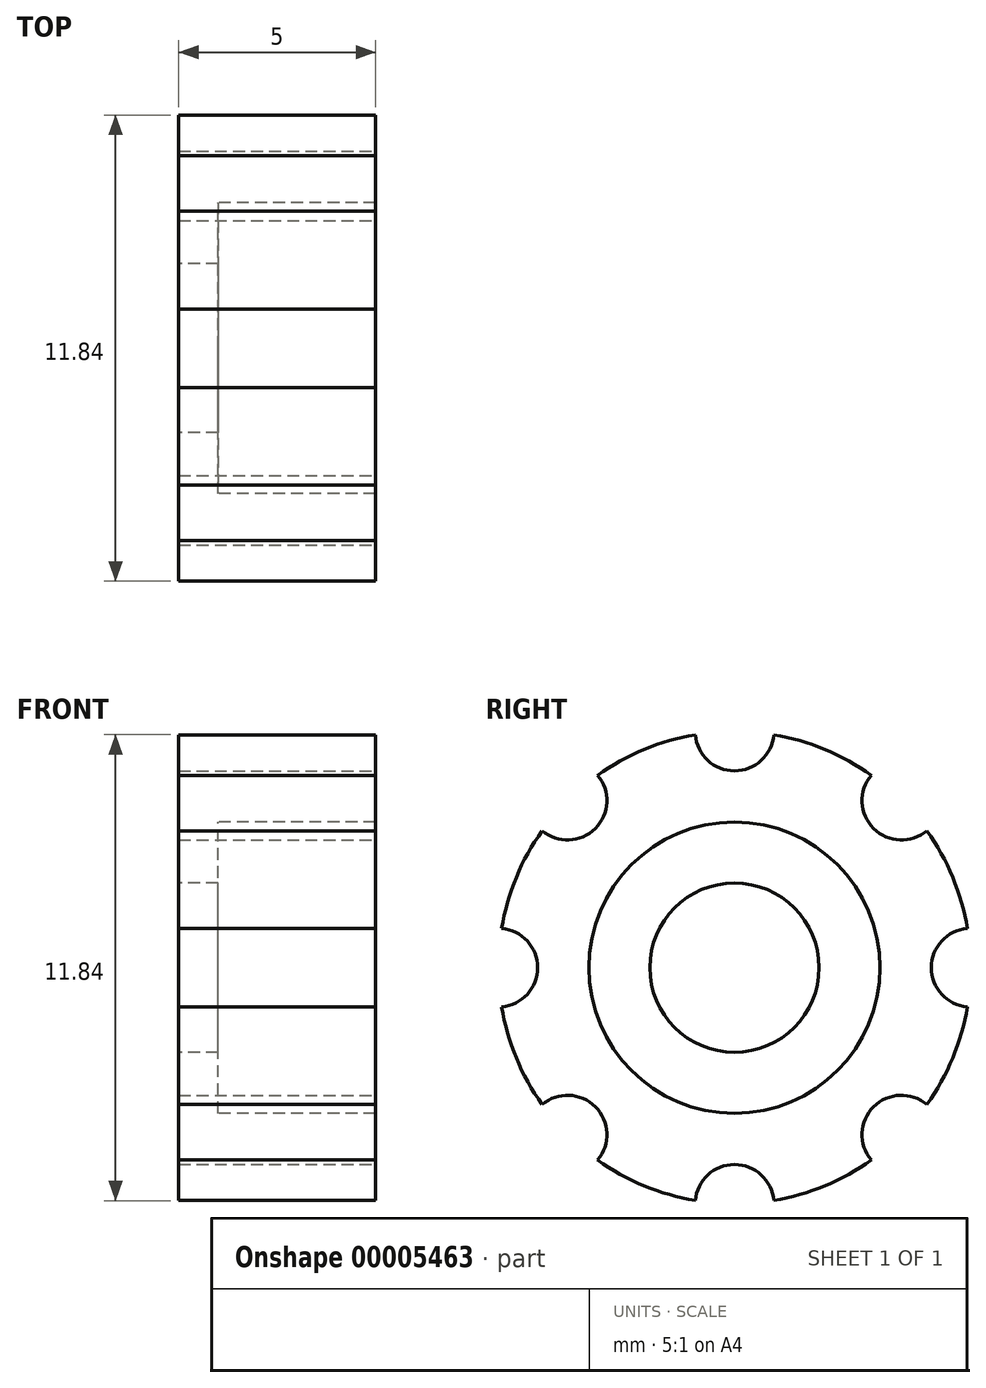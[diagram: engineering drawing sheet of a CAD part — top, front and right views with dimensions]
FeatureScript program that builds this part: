
annotation { "Feature Type Name" : "Feature", "Feature Type Description" : "" }
export const myFeature = defineFeature(function(context is Context, id is Id, definition is map)
    precondition{}
    {
        {
            var Q0;
            Q0=qCreatedBy(makeId("Right.planeOp"),FACE);
            var sketch = newSketch(context, id + "F0", { "sketchPlane" : qUnion([Q0])});
            skCircle(sketch, "E0", {"center": v(0, 0) * mm, "radius": 3.7 * mm});
            skCircle(sketch, "E1", {"center": v(0, 0) * mm, "radius": 6 * mm});
            skCircle(sketch, "E2", {"center": v(0, 0) * mm, "radius": 2.15 * mm});
            skSolve(sketch);
        }
        {
            var Q0;
            Q0=makeQuery(id+"F0.imprint","IMPRINT",FACE,{"disambiguationData":[TD([[makeQuery(id+"F0.imprint","IMPRINT",EDGE,{"derivedFrom":sQuery(id+"F0.wireOp",EDGE,"E1")}),1.0]])]});
            var Q1;
            Q1=makeQuery(id+"F0.imprint","IMPRINT",FACE,{"disambiguationData":[TD([[makeQuery(id+"F0.imprint","IMPRINT",EDGE,{"derivedFrom":sQuery(id+"F0.wireOp",EDGE,"E0")}),-1.0]])]});
            extrude(context, id + "F1", {"entities" : qUnion([Q0, Q1]), "depth" : 5 * mm});
        }
        {
            var Q0;
            Q0=makeQuery(id+"F1.opExtrude","CAP_FACE",FACE,{"disambiguationData":[OSD([sQuery(id+"F0.wireOp",EDGE,"E0"),sQuery(id+"F0.wireOp",EDGE,"E1")])],"isStart":false});
            var sketch = newSketch(context, id + "F2", { "sketchPlane" : qUnion([Q0])});
            skCircle(sketch, "E3", {"center": v(0, -6) * mm, "radius": 1 * mm});
            skLineSegment(sketch, "E4", {"start": v(0, -6) * mm, "end": v(0, 0) * mm, "construction": true});
            skCircle(sketch, "E5.1.0", {"center": v(4.24, -4.24) * mm, "radius": 1 * mm});
            skCircle(sketch, "E5.2.0", {"center": v(6, 0) * mm, "radius": 1 * mm});
            skCircle(sketch, "E5.3.0", {"center": v(4.24, 4.24) * mm, "radius": 1 * mm});
            skCircle(sketch, "E5.4.0", {"center": v(0, 6) * mm, "radius": 1 * mm});
            skCircle(sketch, "E5.5.0", {"center": v(-4.24, 4.24) * mm, "radius": 1 * mm});
            skPoint(sketch, "E5.center", {"position": v(0, 0) * mm});
            skCircle(sketch, "E6.1.6.0", {"center": v(-6, 0) * mm, "radius": 1 * mm});
            skCircle(sketch, "E6.1.7.0", {"center": v(-4.24, -4.24) * mm, "radius": 1 * mm});
            skSolve(sketch);
        }
        {
            var Q0;
            {var subQ0=makeQuery(id+"F1.opExtrude","CAP_EDGE",EDGE,{"disambiguationData":[OSD([sQuery(id+"F0.wireOp",EDGE,"E1")])],"isStart":false});var subQ1=sQuery(id+"F2.wireOp",EDGE,"E5.5.0");var subQ3=makeQuery(id+"F2.imprint","INTERSECT",VERTEX,{"disambiguationData":[OD(0.0)],"derivedFrom":[subQ0,subQ1]});Q0=makeQuery(id+"F2.imprint","IMPRINT",FACE,{"disambiguationData":[TD([[makeQuery(id+"F2.imprint","IMPRINT",EDGE,{"disambiguationData":[TD([[subQ3,-1.0]])],"derivedFrom":subQ1}),1.0]])]});}
            var Q1;
            {var subQ0=makeQuery(id+"F1.opExtrude","CAP_EDGE",EDGE,{"disambiguationData":[OSD([sQuery(id+"F0.wireOp",EDGE,"E1")])],"isStart":false});var subQ1=sQuery(id+"F2.wireOp",EDGE,"E5.4.0");var subQ3=makeQuery(id+"F2.imprint","INTERSECT",VERTEX,{"disambiguationData":[OD(0.0)],"derivedFrom":[subQ0,subQ1]});Q1=makeQuery(id+"F2.imprint","IMPRINT",FACE,{"disambiguationData":[TD([[makeQuery(id+"F2.imprint","IMPRINT",EDGE,{"disambiguationData":[TD([[subQ3,-1.0]])],"derivedFrom":subQ1}),1.0]])]});}
            var Q2;
            {var subQ0=makeQuery(id+"F1.opExtrude","CAP_EDGE",EDGE,{"disambiguationData":[OSD([sQuery(id+"F0.wireOp",EDGE,"E1")])],"isStart":false});var subQ1=sQuery(id+"F2.wireOp",EDGE,"E5.2.0");var subQ3=makeQuery(id+"F2.imprint","INTERSECT",VERTEX,{"disambiguationData":[OD(0.0)],"derivedFrom":[subQ0,subQ1]});Q2=makeQuery(id+"F2.imprint","IMPRINT",FACE,{"disambiguationData":[TD([[makeQuery(id+"F2.imprint","IMPRINT",EDGE,{"disambiguationData":[TD([[subQ3,1.0]])],"derivedFrom":subQ1}),1.0]])]});}
            var Q3;
            {var subQ0=makeQuery(id+"F1.opExtrude","CAP_EDGE",EDGE,{"disambiguationData":[OSD([sQuery(id+"F0.wireOp",EDGE,"E1")])],"isStart":false});var subQ1=sQuery(id+"F2.wireOp",EDGE,"E5.1.0");var subQ3=makeQuery(id+"F2.imprint","INTERSECT",VERTEX,{"disambiguationData":[OD(0.0)],"derivedFrom":[subQ0,subQ1]});Q3=makeQuery(id+"F2.imprint","IMPRINT",FACE,{"disambiguationData":[TD([[makeQuery(id+"F2.imprint","IMPRINT",EDGE,{"disambiguationData":[TD([[subQ3,1.0]])],"derivedFrom":subQ1}),1.0]])]});}
            var Q4;
            {var subQ0=makeQuery(id+"F1.opExtrude","CAP_EDGE",EDGE,{"disambiguationData":[OSD([sQuery(id+"F0.wireOp",EDGE,"E1")])],"isStart":false});var subQ1=sQuery(id+"F2.wireOp",EDGE,"07d8d19e-cda2-4d9f-9653-dbfe602d6117.1.6.0");var subQ3=makeQuery(id+"F2.imprint","INTERSECT",VERTEX,{"disambiguationData":[OD(0.0)],"derivedFrom":[subQ0,subQ1]});Q4=makeQuery(id+"F2.imprint","IMPRINT",FACE,{"disambiguationData":[TD([[makeQuery(id+"F2.imprint","IMPRINT",EDGE,{"disambiguationData":[TD([[subQ3,-1.0]])],"derivedFrom":subQ1}),1.0]])]});}
            var Q5;
            {var subQ0=makeQuery(id+"F1.opExtrude","CAP_EDGE",EDGE,{"disambiguationData":[OSD([sQuery(id+"F0.wireOp",EDGE,"E1")])],"isStart":false});var subQ1=sQuery(id+"F2.wireOp",EDGE,"E5.3.0");var subQ3=makeQuery(id+"F2.imprint","INTERSECT",VERTEX,{"disambiguationData":[OD(0.0)],"derivedFrom":[subQ0,subQ1]});Q5=makeQuery(id+"F2.imprint","IMPRINT",FACE,{"disambiguationData":[TD([[makeQuery(id+"F2.imprint","IMPRINT",EDGE,{"disambiguationData":[TD([[subQ3,-1.0]])],"derivedFrom":subQ1}),1.0]])]});}
            var Q6;
            {var subQ0=makeQuery(id+"F1.opExtrude","CAP_EDGE",EDGE,{"disambiguationData":[OSD([sQuery(id+"F0.wireOp",EDGE,"E1")])],"isStart":false});var subQ1=sQuery(id+"F2.wireOp",EDGE,"E3");var subQ3=makeQuery(id+"F2.imprint","INTERSECT",VERTEX,{"disambiguationData":[OD(0.0)],"derivedFrom":[subQ0,subQ1]});Q6=makeQuery(id+"F2.imprint","IMPRINT",FACE,{"disambiguationData":[TD([[makeQuery(id+"F2.imprint","IMPRINT",EDGE,{"disambiguationData":[TD([[subQ3,1.0]])],"derivedFrom":subQ1}),1.0]])]});}
            var Q7;
            {var subQ0=makeQuery(id+"F1.opExtrude","CAP_EDGE",EDGE,{"disambiguationData":[OSD([sQuery(id+"F0.wireOp",EDGE,"E1")])],"isStart":false});var subQ1=sQuery(id+"F2.wireOp",EDGE,"07d8d19e-cda2-4d9f-9653-dbfe602d6117.1.7.0");var subQ3=makeQuery(id+"F2.imprint","INTERSECT",VERTEX,{"disambiguationData":[OD(0.0)],"derivedFrom":[subQ0,subQ1]});Q7=makeQuery(id+"F2.imprint","IMPRINT",FACE,{"disambiguationData":[TD([[makeQuery(id+"F2.imprint","IMPRINT",EDGE,{"disambiguationData":[TD([[subQ3,1.0]])],"derivedFrom":subQ1}),1.0]])]});}
            var Q8;
            {var subQ0=sQuery(id+"F2.wireOp",EDGE,"E6.1.7.0");var subQ1=makeQuery(id+"F1.opExtrude","CAP_EDGE",EDGE,{"disambiguationData":[OSD([sQuery(id+"F0.wireOp",EDGE,"E1")])],"isStart":false});var subQ2=makeQuery(id+"F2.imprint","INTERSECT",VERTEX,{"disambiguationData":[OD(0.0)],"derivedFrom":[subQ1,subQ0]});Q8=makeQuery(id+"F2.imprint","IMPRINT",FACE,{"disambiguationData":[TD([[makeQuery(id+"F2.imprint","IMPRINT",EDGE,{"disambiguationData":[TD([[subQ2,-1.0]])],"derivedFrom":subQ0}),1.0]])]});}
            var Q9;
            {var subQ0=sQuery(id+"F2.wireOp",EDGE,"E6.1.6.0");var subQ1=makeQuery(id+"F1.opExtrude","CAP_EDGE",EDGE,{"disambiguationData":[OSD([sQuery(id+"F0.wireOp",EDGE,"E1")])],"isStart":false});var subQ2=makeQuery(id+"F2.imprint","INTERSECT",VERTEX,{"disambiguationData":[OD(0.0)],"derivedFrom":[subQ1,subQ0]});Q9=makeQuery(id+"F2.imprint","IMPRINT",FACE,{"disambiguationData":[TD([[makeQuery(id+"F2.imprint","IMPRINT",EDGE,{"disambiguationData":[TD([[subQ2,-1.0]])],"derivedFrom":subQ0}),1.0]])]});}
            var Q10;
            {var subQ0=sQuery(id+"F2.wireOp",EDGE,"E6.1.6.0");var subQ1=makeQuery(id+"F1.opExtrude","CAP_EDGE",EDGE,{"disambiguationData":[OSD([sQuery(id+"F0.wireOp",EDGE,"E1")])],"isStart":false});var subQ2=makeQuery(id+"F2.imprint","INTERSECT",VERTEX,{"disambiguationData":[OD(0.0)],"derivedFrom":[subQ1,subQ0]});Q10=makeQuery(id+"F2.imprint","IMPRINT",FACE,{"disambiguationData":[TD([[makeQuery(id+"F2.imprint","IMPRINT",EDGE,{"disambiguationData":[TD([[subQ2,1.0]])],"derivedFrom":subQ0}),1.0]])]});}
            var Q11;
            {var subQ0=sQuery(id+"F2.wireOp",EDGE,"E6.1.7.0");var subQ1=makeQuery(id+"F1.opExtrude","CAP_EDGE",EDGE,{"disambiguationData":[OSD([sQuery(id+"F0.wireOp",EDGE,"E1")])],"isStart":false});var subQ2=makeQuery(id+"F2.imprint","INTERSECT",VERTEX,{"disambiguationData":[OD(0.0)],"derivedFrom":[subQ1,subQ0]});Q11=makeQuery(id+"F2.imprint","IMPRINT",FACE,{"disambiguationData":[TD([[makeQuery(id+"F2.imprint","IMPRINT",EDGE,{"disambiguationData":[TD([[subQ2,1.0]])],"derivedFrom":subQ0}),1.0]])]});}
            extrude(context, id + "F3", {"entities" : qUnion([Q0, Q1, Q2, Q3, Q4, Q5, Q6, Q7, Q8, Q9, Q10, Q11]), "operationType" : NewBodyOperationType.REMOVE, "endBound" : BoundingType.THROUGH_ALL, "oppositeDirection" : true, "depth" : 25 * mm});
        }
        {
            var Q0;
            Q0=makeQuery(id+"F0.imprint","IMPRINT",FACE,{"disambiguationData":[TD([[makeQuery(id+"F0.imprint","IMPRINT",EDGE,{"derivedFrom":sQuery(id+"F0.wireOp",EDGE,"E0")}),1.0]])]});
            extrude(context, id + "F4", {"entities" : qUnion([Q0]), "operationType" : NewBodyOperationType.ADD, "depth" : 1 * mm});
        }
    });
